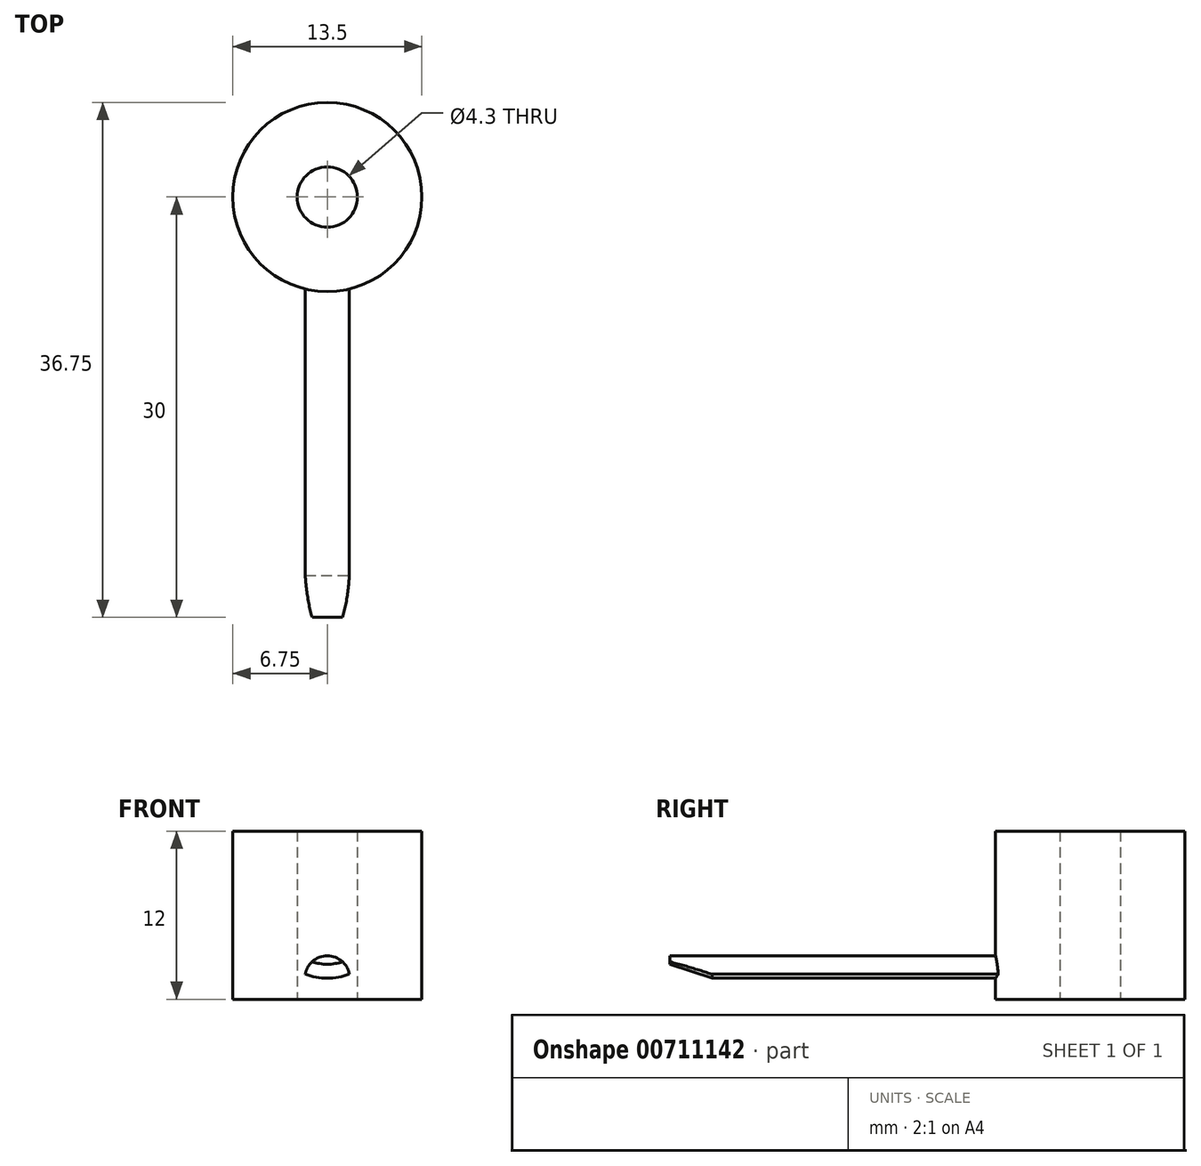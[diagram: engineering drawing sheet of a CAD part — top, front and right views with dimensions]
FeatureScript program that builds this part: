
annotation { "Feature Type Name" : "Feature", "Feature Type Description" : "" }
export const myFeature = defineFeature(function(context is Context, id is Id, definition is map)
    precondition{}
    {
        {
            var Q0;
            Q0=qCreatedBy(makeId("Top.planeOp"),FACE);
            var sketch = newSketch(context, id + "F0", { "sketchPlane" : qUnion([Q0])});
            skCircle(sketch, "E0", {"center": v(0, 0) * mm, "radius": 6.75 * mm});
            skCircle(sketch, "E1", {"center": v(0, 0) * mm, "radius": 2.15 * mm});
            skSolve(sketch);
        }
        {
            var Q0;
            Q0=makeQuery(id+"F0.imprint","IMPRINT",FACE,{"disambiguationData":[TD([[makeQuery(id+"F0.imprint","IMPRINT",EDGE,{"derivedFrom":sQuery(id+"F0.wireOp",EDGE,"E0")}),1.0]])]});
            extrude(context, id + "F1", {"entities" : qUnion([Q0]), "depth" : 6 * mm, "offsetDistance" : 25 * mm, "hasSecondDirection" : true, "secondDirectionOppositeDirection" : true, "secondDirectionDepth" : 6 * mm});
        }
        {
            var Q0;
            Q0=qCreatedBy(makeId("Front.planeOp"),FACE);
            var sketch = newSketch(context, id + "F2", { "sketchPlane" : qUnion([Q0])});
            skCircle(sketch, "E2", {"center": v(0, 0) * mm, "radius": 4.5 * mm});
            skArc(sketch, "E3", {"start": v(-1.57, -4.22) * mm, "mid": v(0, -2.9) * mm, "end": v(1.57, -4.22) * mm});
            skSolve(sketch);
        }
        {
            var Q0;
            {var subQ0=sQuery(id+"F2.wireOp",EDGE,"E3");Q0=makeQuery(id+"F2.imprint","IMPRINT",FACE,{"disambiguationData":[TD([[makeQuery(id+"F2.imprint","IMPRINT",EDGE,{"derivedFrom":subQ0}),1.0]])]});}
            extrude(context, id + "F3", {"entities" : qUnion([Q0]), "operationType" : NewBodyOperationType.ADD, "depth" : 30 * mm, "offsetDistance" : 25 * mm, "hasSecondDirection" : true, "secondDirectionOppositeDirection" : false, "secondDirectionDepth" : 5 * mm});
        }
        {
            var Q0;
            Q0=makeQuery(id+"F3.opExtrude","CAP_EDGE",EDGE,{"disambiguationData":[OSD([sQuery(id+"F2.wireOp",EDGE,"E2")])],"isStart":false});
            chamfer(context, id + "F4", {"entities" : qUnion([Q0]), "chamferType" : ChamferType.TWO_OFFSETS, "width1" : 1 * mm, "oppositeDirection" : false, "width2" : 3 * mm, "tangentPropagation" : true});
        }
    });
